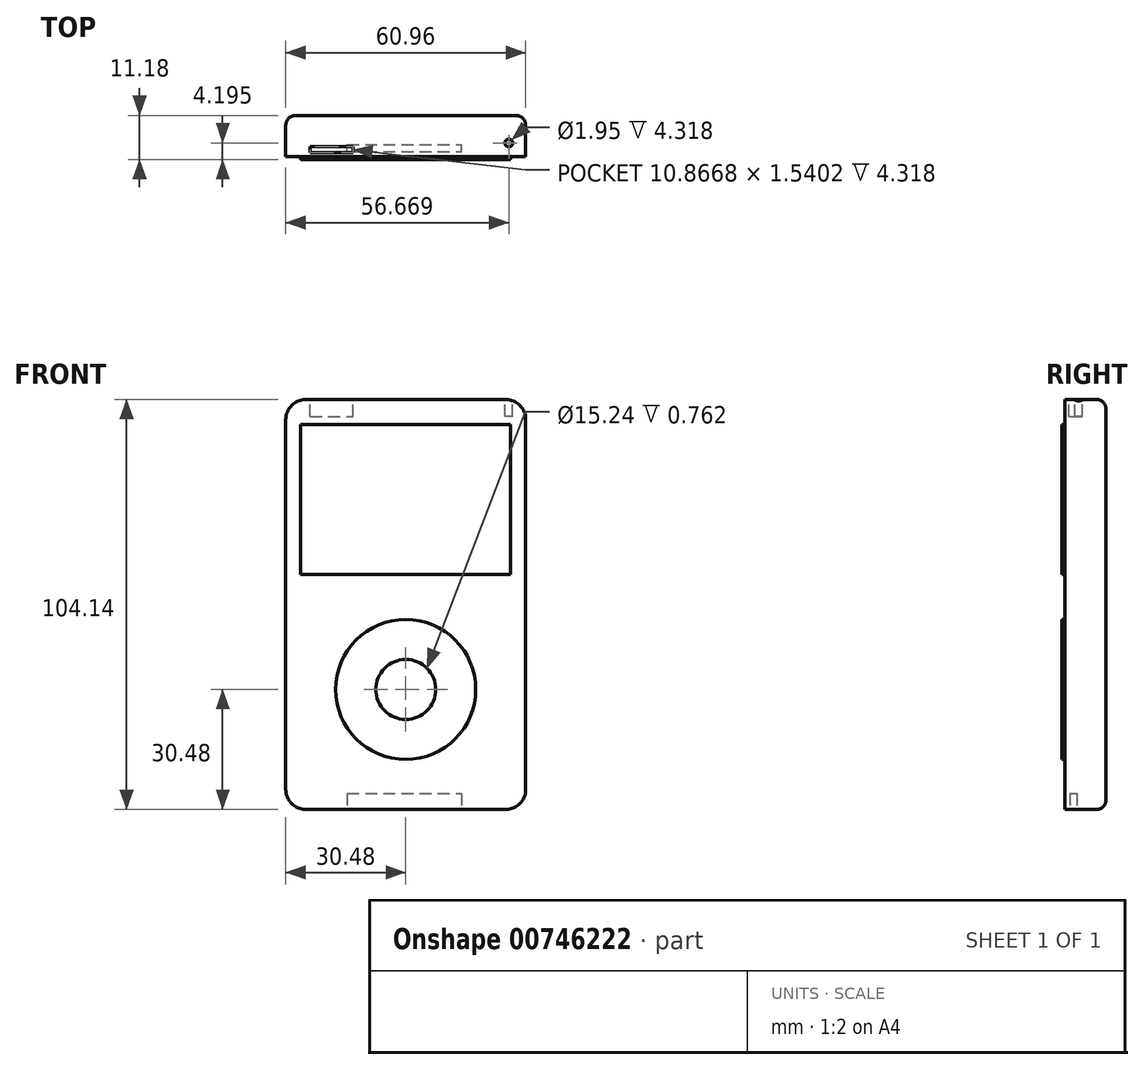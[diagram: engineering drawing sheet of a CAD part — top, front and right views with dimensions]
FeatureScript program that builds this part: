
annotation { "Feature Type Name" : "Feature", "Feature Type Description" : "" }
export const myFeature = defineFeature(function(context is Context, id is Id, definition is map)
    precondition{}
    {
        {
            var Q0;
            Q0=qCreatedBy(makeId("Front.planeOp"),FACE);
            var sketch = newSketch(context, id + "F0", { "sketchPlane" : qUnion([Q0])});
            skLineSegment(sketch, "E0.bottom", {"start": v(0, 0) * mm, "end": v(60.96, 0) * mm});
            skLineSegment(sketch, "E0.top", {"start": v(0, -104.14) * mm, "end": v(60.96, -104.14) * mm});
            skLineSegment(sketch, "E0.left", {"start": v(0, 0) * mm, "end": v(0, -104.14) * mm});
            skLineSegment(sketch, "E0.right", {"start": v(60.96, 0) * mm, "end": v(60.96, -104.14) * mm});
            skSolve(sketch);
        }
        {
            var Q0;
            Q0=makeQuery(id+"F0.imprint","IMPRINT",FACE,{"disambiguationData":[TD([[makeQuery(id+"F0.imprint","IMPRINT",EDGE,{"derivedFrom":sQuery(id+"F0.wireOp",EDGE,"E0.bottom")}),-1.0]])]});
            extrude(context, id + "F1", {"entities" : qUnion([Q0]), "depth" : 10.4 * mm, "offsetDistance" : 25.4 * mm});
        }
        {
            var Q0;
            Q0=makeQuery(id+"F1.opExtrude","SWEPT_EDGE",EDGE,{"disambiguationData":[OSD([sQuery(id+"F0.wireOp",EDGE,"E0.bottom"),sQuery(id+"F0.wireOp",EDGE,"E0.right")])]});
            var Q1;
            Q1=makeQuery(id+"F1.opExtrude","SWEPT_EDGE",EDGE,{"disambiguationData":[OSD([sQuery(id+"F0.wireOp",EDGE,"E0.bottom"),sQuery(id+"F0.wireOp",EDGE,"E0.left")])]});
            var Q2;
            Q2=makeQuery(id+"F1.opExtrude","SWEPT_EDGE",EDGE,{"disambiguationData":[OSD([sQuery(id+"F0.wireOp",EDGE,"E0.top"),sQuery(id+"F0.wireOp",EDGE,"E0.left")])]});
            var Q3;
            Q3=makeQuery(id+"F1.opExtrude","SWEPT_EDGE",EDGE,{"disambiguationData":[OSD([sQuery(id+"F0.wireOp",EDGE,"E0.top"),sQuery(id+"F0.wireOp",EDGE,"E0.right")])]});
            fillet(context, id + "F2", {"entities" : qUnion([Q0, Q1, Q2, Q3]), "radius" : 5.08 * mm, "tangentPropagation" : true, "allowEdgeOverflow" : false});
        }
        {
            var Q0;
            Q0=makeQuery(id+"F1.opExtrude","CAP_FACE",FACE,{"disambiguationData":[OSD([sQuery(id+"F0.wireOp",EDGE,"E0.bottom"),sQuery(id+"F0.wireOp",EDGE,"E0.top"),sQuery(id+"F0.wireOp",EDGE,"E0.left"),sQuery(id+"F0.wireOp",EDGE,"E0.right")])],"isStart":false});
            var sketch = newSketch(context, id + "F3", { "sketchPlane" : qUnion([Q0])});
            skCircle(sketch, "E1", {"center": v(30.48, -73.66) * mm, "radius": 7.62 * mm});
            skPoint(sketch, "E1.centerSnap0", {"position": v(30.48, -104.14) * mm});
            skCircle(sketch, "E2", {"center": v(30.48, -73.66) * mm, "radius": 17.78 * mm});
            skLineSegment(sketch, "E3.bottom", {"start": v(3.8, -6.35) * mm, "end": v(57.15, -6.35) * mm});
            skLineSegment(sketch, "E3.top", {"start": v(3.8, -44.45) * mm, "end": v(57.15, -44.45) * mm});
            skLineSegment(sketch, "E3.left", {"start": v(3.8, -6.35) * mm, "end": v(3.8, -44.45) * mm});
            skLineSegment(sketch, "E3.right", {"start": v(57.15, -6.35) * mm, "end": v(57.15, -44.45) * mm});
            skPoint(sketch, "E3.middle", {"position": v(30.48, -25.4) * mm});
            skSolve(sketch);
        }
        {
            var Q0;
            Q0=makeQuery(id+"F3.imprint","IMPRINT",FACE,{"disambiguationData":[TD([[makeQuery(id+"F3.imprint","IMPRINT",EDGE,{"derivedFrom":sQuery(id+"F3.wireOp",EDGE,"E3.bottom")}),-1.0]])]});
            var Q1;
            Q1=makeQuery(id+"F3.imprint","IMPRINT",FACE,{"disambiguationData":[TD([[makeQuery(id+"F3.imprint","IMPRINT",EDGE,{"derivedFrom":sQuery(id+"F3.wireOp",EDGE,"E1")}),-1.0]])]});
            extrude(context, id + "F4", {"entities" : qUnion([Q0, Q1]), "operationType" : NewBodyOperationType.ADD, "depth" : 0.76 * mm, "offsetDistance" : 25.4 * mm});
        }
        {
            var Q0;
            {var subQ0=sQuery(id+"F0.wireOp",EDGE,"E0.left");var subQ1=sQuery(id+"F0.wireOp",EDGE,"E0.bottom");Q0=makeQuery(id+"F2.opFillet","BLEND_EDGE",EDGE,{"blendedFrom":[makeQuery(id+"F1.opExtrude","SWEPT_EDGE",EDGE,{"disambiguationData":[OSD([subQ1,subQ0])]}),makeQuery(id+"F1.opExtrude","CAP_FACE",FACE,{"disambiguationData":[OSD([subQ1,sQuery(id+"F0.wireOp",EDGE,"E0.top"),subQ0,sQuery(id+"F0.wireOp",EDGE,"E0.right")])],"isStart":true})],"blendedInto":[makeQuery(id+"F1.opExtrude","CAP_FACE",FACE,{"disambiguationData":[OSD([subQ1,sQuery(id+"F0.wireOp",EDGE,"E0.top"),subQ0,sQuery(id+"F0.wireOp",EDGE,"E0.right")])],"isStart":true})]});}
            fillet(context, id + "F5", {"entities" : qUnion([Q0]), "radius" : 2.45 * mm, "tangentPropagation" : true, "allowEdgeOverflow" : false});
        }
        {
            var Q0;
            Q0=makeQuery(id+"F1.opExtrude","SWEPT_FACE",FACE,{"disambiguationData":[OSD([sQuery(id+"F0.wireOp",EDGE,"E0.bottom")])]});
            var sketch = newSketch(context, id + "F6", { "sketchPlane" : qUnion([Q0])});
            skSolve(sketch);
        }
        {
            var Q0;
            {var subQ0=sQuery(id+"F0.wireOp",EDGE,"E0.bottom");Q0=makeQuery(id+"F6.imprint","IMPRINT",FACE,{"disambiguationData":[TD([[makeQuery(id+"F6.imprint","IMPRINT",EDGE,{"derivedFrom":makeQuery(id+"F1.opExtrude","CAP_EDGE",EDGE,{"disambiguationData":[OSD([subQ0])],"isStart":false})}),1.0]])]});}
            var sketch = newSketch(context, id + "F7", { "sketchPlane" : qUnion([Q0])});
            skCircle(sketch, "E4", {"center": v(56.67, -6.99) * mm, "radius": 0.98 * mm});
            skLineSegment(sketch, "E5.bottom", {"start": v(6.19, -9.47) * mm, "end": v(17.05, -9.47) * mm});
            skLineSegment(sketch, "E5.top", {"start": v(6.19, -7.93) * mm, "end": v(17.05, -7.93) * mm});
            skLineSegment(sketch, "E5.left", {"start": v(6.19, -9.47) * mm, "end": v(6.19, -7.93) * mm});
            skLineSegment(sketch, "E5.right", {"start": v(17.05, -9.47) * mm, "end": v(17.05, -7.93) * mm});
            skSolve(sketch);
        }
        {
            var Q0;
            Q0 = qSketchRegion(id + "F7", true);
            extrude(context, id + "F8", {"entities" : qUnion([Q0]), "operationType" : NewBodyOperationType.REMOVE, "oppositeDirection" : true, "depth" : 4.32 * mm, "offsetDistance" : 25.4 * mm});
        }
        {
            var Q0;
            Q0=makeQuery(id+"F1.opExtrude","SWEPT_FACE",FACE,{"disambiguationData":[OSD([sQuery(id+"F0.wireOp",EDGE,"E0.top")])]});
            var sketch = newSketch(context, id + "F9", { "sketchPlane" : qUnion([Q0])});
            skLineSegment(sketch, "E6.bottom", {"start": v(15.6, 9.14) * mm, "end": v(44.61, 9.14) * mm});
            skLineSegment(sketch, "E6.top", {"start": v(15.6, 7.42) * mm, "end": v(44.61, 7.42) * mm});
            skLineSegment(sketch, "E6.left", {"start": v(15.6, 9.14) * mm, "end": v(15.6, 7.42) * mm});
            skLineSegment(sketch, "E6.right", {"start": v(44.61, 9.14) * mm, "end": v(44.61, 7.42) * mm});
            skSolve(sketch);
        }
        {
            var Q0;
            Q0=makeQuery(id+"F9.imprint","IMPRINT",FACE,{"disambiguationData":[TD([[makeQuery(id+"F9.imprint","IMPRINT",EDGE,{"derivedFrom":sQuery(id+"F9.wireOp",EDGE,"E6.bottom")}),-1.0]])]});
            extrude(context, id + "F10", {"entities" : qUnion([Q0]), "operationType" : NewBodyOperationType.REMOVE, "oppositeDirection" : true, "depth" : 4.06 * mm, "offsetDistance" : 25.4 * mm});
        }
    });
